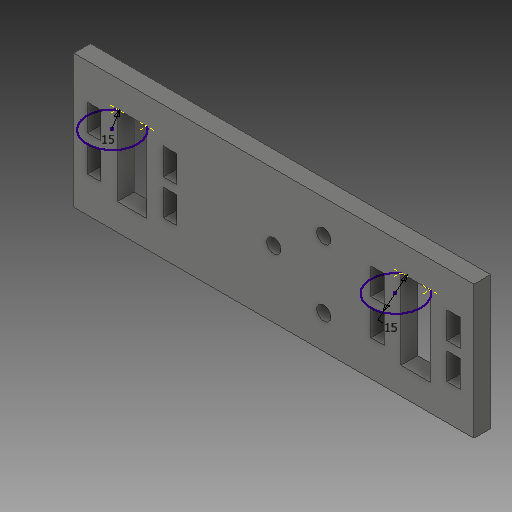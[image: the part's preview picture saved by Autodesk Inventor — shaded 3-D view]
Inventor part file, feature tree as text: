
AUTODESK INVENTOR PART (.ipt)
format: ipt  version: 2019 (Build 230136000, 136)  size: 168,960 bytes
history: native  units: in
note: dims shown in document units (in); Inventor stores cm internally (conversion verified against a paired STEP export)
features: sketch x2, extrude x1
ambient origin geometry x8: Origin, YZ Plane, XZ Plane, XY Plane, X Axis, Y Axis, Z Axis, Center Point
bodies: Solid1 (feature_tree)
feature tree (3):
  extrude  "Extrusion1"  Depth=1.5748in
  sketch  "Sketch2"  dims[d2=0.3465in d3=0.9449in d4=0.3465in d5=0.9449in d6=0.1575in d7=0.315in d8=0.1969in d9=0.1969in d10=0.0in d11=3.0in d12=0.5906in d13=0.5906in d14=0.1673in d15=0.1673in d16=0.7874in d17=1.7717in d18=0.1673in]
  sketch  "Sketch1"  dims[d0=4.7244in d1=1.5748in]
